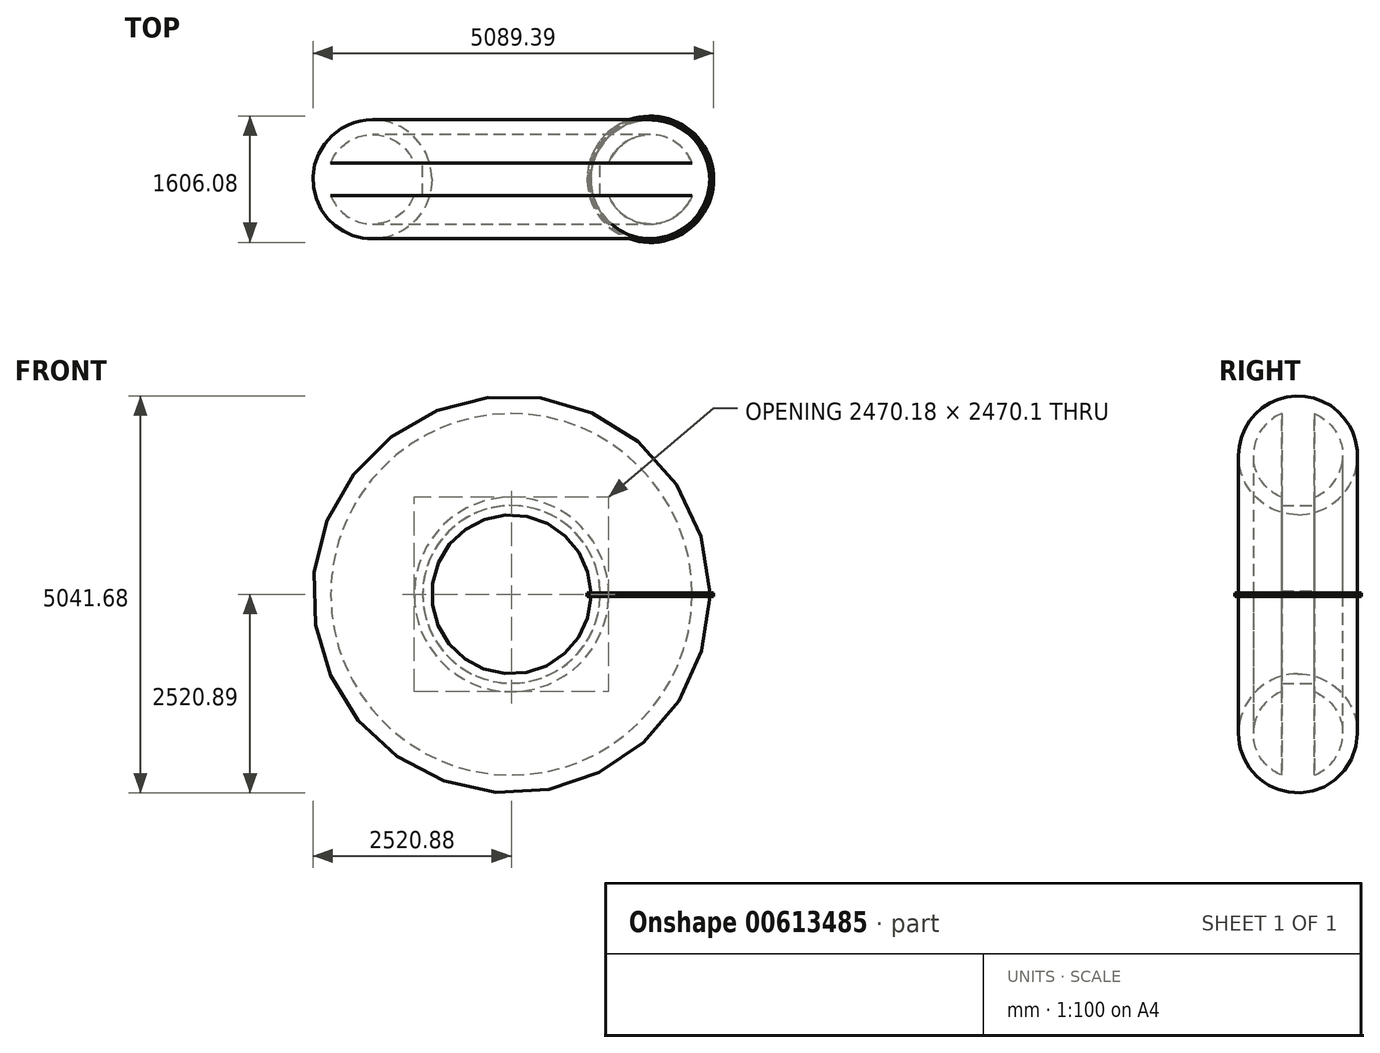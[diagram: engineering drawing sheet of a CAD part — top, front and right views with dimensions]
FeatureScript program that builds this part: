
annotation { "Feature Type Name" : "Feature", "Feature Type Description" : "" }
export const myFeature = defineFeature(function(context is Context, id is Id, definition is map)
    precondition{}
    {
        {
            var Q0;
            Q0=qCreatedBy(makeId("Front.planeOp"),FACE);
            var sketch = newSketch(context, id + "F0", { "sketchPlane" : qUnion([Q0])});
            skLineSegment(sketch, "E0.bottom", {"start": v(-117.21, -26.35) * mm, "end": v(117.21, -26.35) * mm});
            skLineSegment(sketch, "E0.top", {"start": v(-117.21, 26.35) * mm, "end": v(117.21, 26.35) * mm});
            skLineSegment(sketch, "E0.left", {"start": v(-117.21, -26.35) * mm, "end": v(-117.21, 26.35) * mm});
            skLineSegment(sketch, "E0.right", {"start": v(117.21, -26.35) * mm, "end": v(117.21, 26.35) * mm});
            skPoint(sketch, "E0.middle", {"position": v(0, 0) * mm});
            skCircle(sketch, "E1.cCircle", {"center": v(-80.9, 0) * mm, "radius": 19.3 * mm, "construction": true});
            skLineSegment(sketch, "E1.0", {"start": v(-100.2, -8) * mm, "end": v(-100.2, 8) * mm});
            skLineSegment(sketch, "E1.1", {"start": v(-100.2, 8) * mm, "end": v(-88.9, 19.3) * mm});
            skLineSegment(sketch, "E1.2", {"start": v(-88.9, 19.3) * mm, "end": v(-72.92, 19.3) * mm});
            skLineSegment(sketch, "E1.3", {"start": v(-72.92, 19.3) * mm, "end": v(-61.61, 8) * mm});
            skLineSegment(sketch, "E1.4", {"start": v(-61.61, 8) * mm, "end": v(-61.61, -8) * mm});
            skLineSegment(sketch, "E1.5", {"start": v(-61.61, -8) * mm, "end": v(-72.92, -19.3) * mm});
            skLineSegment(sketch, "E1.6", {"start": v(-72.92, -19.3) * mm, "end": v(-88.9, -19.3) * mm});
            skLineSegment(sketch, "E1.7", {"start": v(-88.9, -19.3) * mm, "end": v(-100.2, -8) * mm});
            skPoint(sketch, "E1.0.midPoint", {"position": v(-100.2, 0) * mm});
            skSolve(sketch);
        }
        {
            var Q0;
            Q0=makeQuery(id+"F0.imprint","IMPRINT",FACE,{"disambiguationData":[TD([[makeQuery(id+"F0.imprint","IMPRINT",EDGE,{"derivedFrom":sQuery(id+"F0.wireOp",EDGE,"E0.bottom")}),1.0]])]});
            extrude(context, id + "F1", {"entities" : qUnion([Q0]), "depth" : 14.82 * mm, "offsetDistance" : 25.4 * mm});
        }
        {
            var Q0;
            Q0=qCreatedBy(makeId("Top.planeOp"),FACE);
            var sketch = newSketch(context, id + "F2", { "sketchPlane" : qUnion([Q0])});
            skCircle(sketch, "E2", {"center": v(685.69, 0) * mm, "radius": 594.25 * mm});
            skSolve(sketch);
        }
        {
            var Q0;
            Q0=makeQuery(id+"F1.opExtrude","SWEPT_FACE",FACE,{"disambiguationData":[OSD([sQuery(id+"F0.wireOp",EDGE,"E0.top")])]});
            extrude(context, id + "F3", {"entities" : qUnion([Q0]), "operationType" : NewBodyOperationType.REMOVE, "oppositeDirection" : true, "depth" : 10.5 * mm, "offsetDistance" : 25.4 * mm});
        }
        {
            var Q0;
            Q0=makeQuery(id+"F1.opExtrude","CAP_FACE",FACE,{"disambiguationData":[OSD([sQuery(id+"F0.wireOp",EDGE,"E0.bottom"),sQuery(id+"F0.wireOp",EDGE,"E0.top"),sQuery(id+"F0.wireOp",EDGE,"E0.left"),sQuery(id+"F0.wireOp",EDGE,"E0.right"),sQuery(id+"F0.wireOp",EDGE,"E1.0"),sQuery(id+"F0.wireOp",EDGE,"E1.1"),sQuery(id+"F0.wireOp",EDGE,"E1.2"),sQuery(id+"F0.wireOp",EDGE,"E1.3"),sQuery(id+"F0.wireOp",EDGE,"E1.4"),sQuery(id+"F0.wireOp",EDGE,"E1.5"),sQuery(id+"F0.wireOp",EDGE,"E1.6"),sQuery(id+"F0.wireOp",EDGE,"E1.7")])],"isStart":false});
            var Q1;
            Q1=sQuery(id+"F2.wireOp",EDGE,"E2");
            revolve(context, id + "F4", {"operationType" : NewBodyOperationType.ADD, "entities" : qUnion([Q0]), "axis" : qUnion([Q1]), "revolveType" : RevolveType.FULL});
        }
        {
            var Q0;
            {var subQ8=sQuery(id+"F0.wireOp",EDGE,"E0.right");var subQ10=sQuery(id+"F0.wireOp",EDGE,"E0.top");var subQ13=makeQuery(id+"F1.opExtrude","SWEPT_FACE",FACE,{"disambiguationData":[OSD([subQ8])]});var subQ15=makeQuery(id+"F3.opExtrude","CAP_FACE",FACE,{"disambiguationData":[OSD([subQ10])],"isStart":false});Q0=makeQuery(id+"F4.boolean.opBoolean","MERGE",FACE,{"derivedFrom":[makeQuery(id+"F3.boolean.opBoolean","COPY",FACE,{"disambiguationData":[TD([subQ13])],"derivedFrom":subQ15}),makeQuery(id+"F4.opRevolve","SWEPT_FACE",FACE,{"disambiguationData":[OSD([subQ10]),TDD([makeQuery(id+"F3.boolean.opBoolean","COPY",EDGE,{"disambiguationData":[TD([subQ13])],"derivedFrom":makeQuery(id+"F3.opExtrude","CAP_EDGE",EDGE,{"disambiguationData":[OSD([subQ10]),TDD([makeQuery(id+"F1.opExtrude","CAP_EDGE",EDGE,{"disambiguationData":[OSD([subQ10])],"isStart":false})])],"isStart":false})})])]})]});}
            var sketch = newSketch(context, id + "F5", { "sketchPlane" : qUnion([Q0])});
            skLineSegment(sketch, "E3.bottom", {"start": v(47.85, -205.15) * mm, "end": v(1323.53, -205.15) * mm});
            skLineSegment(sketch, "E3.top", {"start": v(47.85, 205.15) * mm, "end": v(1323.53, 205.15) * mm});
            skLineSegment(sketch, "E3.left", {"start": v(47.85, -205.15) * mm, "end": v(47.85, 205.15) * mm});
            skLineSegment(sketch, "E3.right", {"start": v(1323.53, -205.15) * mm, "end": v(1323.53, 205.15) * mm});
            skPoint(sketch, "E3.middle", {"position": v(685.69, 0) * mm});
            skSolve(sketch);
        }
        {
            var Q0;
            Q0 = qSketchRegion(id + "F5", true);
            extrude(context, id + "F6", {"entities" : qUnion([Q0]), "operationType" : NewBodyOperationType.ADD, "depth" : 25.4 * mm, "offsetDistance" : 25.4 * mm});
        }
        {
            var Q0;
            Q0=qCreatedBy(makeId("Front.planeOp"),FACE);
            var sketch = newSketch(context, id + "F7", { "sketchPlane" : qUnion([Q0])});
            skCircle(sketch, "E4", {"center": v(-1079.82, 0) * mm, "radius": 1078.27 * mm});
            skSolve(sketch);
        }
        {
            var Q0;
            {var subQ8=sQuery(id+"F0.wireOp",EDGE,"E0.right");var subQ10=sQuery(id+"F0.wireOp",EDGE,"E0.top");var subQ13=makeQuery(id+"F1.opExtrude","SWEPT_FACE",FACE,{"disambiguationData":[OSD([subQ8])]});var subQ15=makeQuery(id+"F3.opExtrude","CAP_FACE",FACE,{"disambiguationData":[OSD([subQ10])],"isStart":false});Q0=makeQuery(id+"F4.boolean.opBoolean","MERGE",FACE,{"derivedFrom":[makeQuery(id+"F3.boolean.opBoolean","COPY",FACE,{"disambiguationData":[TD([subQ13])],"derivedFrom":subQ15}),makeQuery(id+"F4.opRevolve","SWEPT_FACE",FACE,{"disambiguationData":[OSD([subQ10]),TDD([makeQuery(id+"F3.boolean.opBoolean","COPY",EDGE,{"disambiguationData":[TD([subQ13])],"derivedFrom":makeQuery(id+"F3.opExtrude","CAP_EDGE",EDGE,{"disambiguationData":[OSD([subQ10]),TDD([makeQuery(id+"F1.opExtrude","CAP_EDGE",EDGE,{"disambiguationData":[OSD([subQ10])],"isStart":false})])],"isStart":false})})])]})]});}
            var Q1;
            Q1=makeQuery(id+"F6.opExtrude","CAP_FACE",FACE,{"disambiguationData":[OSD([sQuery(id+"F5.wireOp",EDGE,"E3.bottom"),sQuery(id+"F5.wireOp",EDGE,"E3.top"),sQuery(id+"F5.wireOp",EDGE,"E3.left"),sQuery(id+"F5.wireOp",EDGE,"E3.right")])],"isStart":false});
            var Q2;
            Q2=sQuery(id+"F7.wireOp",EDGE,"E4");
            revolve(context, id + "F8", {"operationType" : NewBodyOperationType.ADD, "entities" : qUnion([Q0, Q1]), "axis" : qUnion([Q2]), "revolveType" : RevolveType.FULL});
        }
    });
